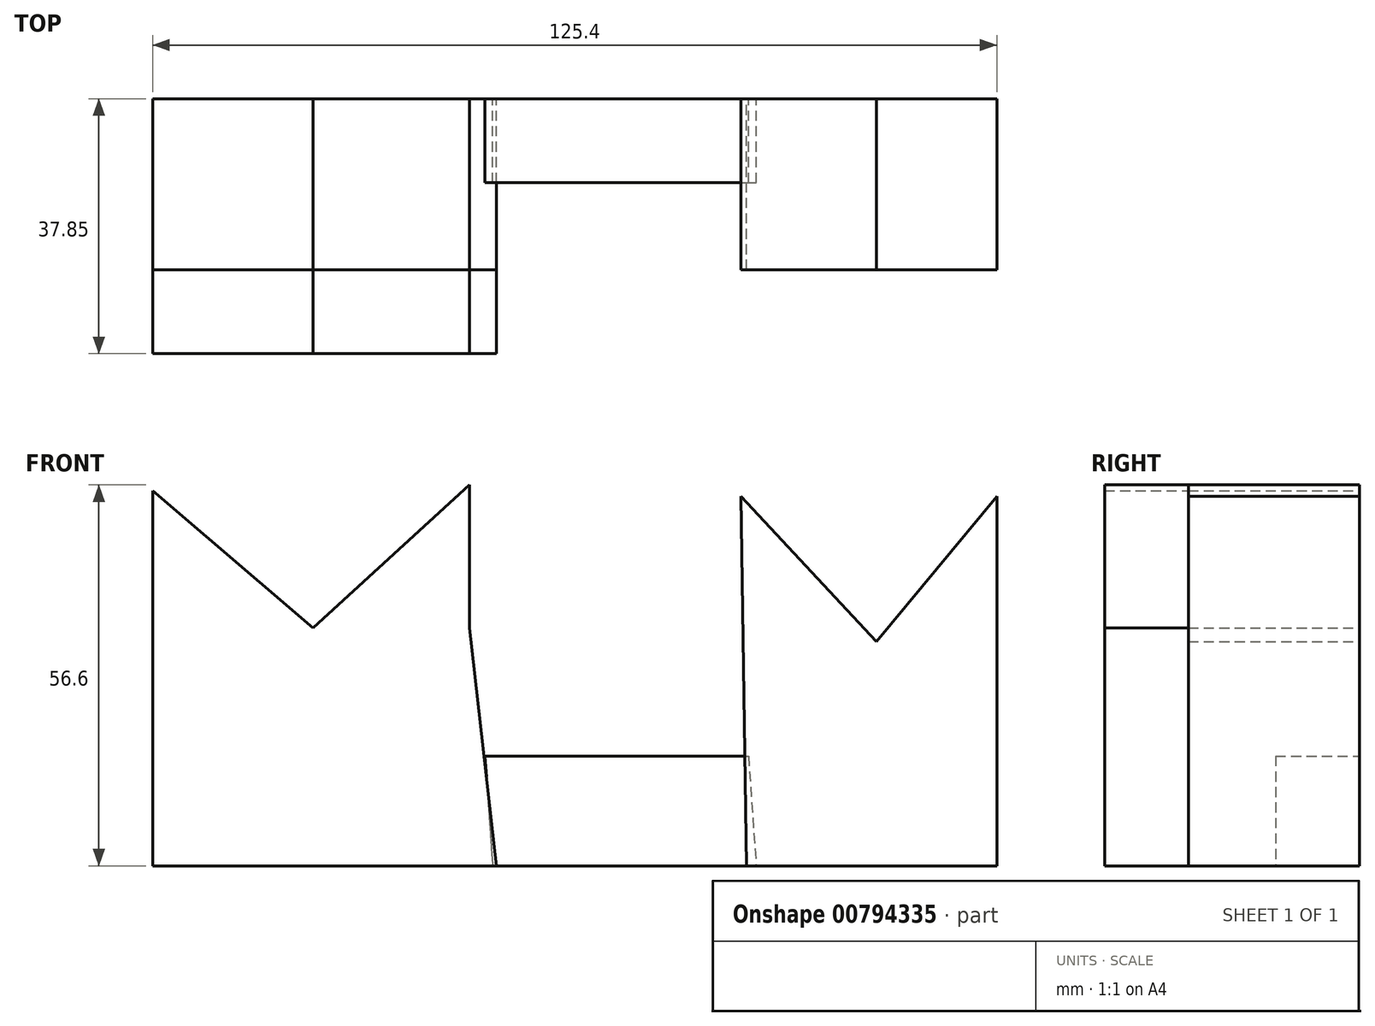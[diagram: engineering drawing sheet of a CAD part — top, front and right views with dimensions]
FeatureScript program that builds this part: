
annotation { "Feature Type Name" : "Feature", "Feature Type Description" : "" }
export const myFeature = defineFeature(function(context is Context, id is Id, definition is map)
    precondition{}
    {
        {
            var Q0;
            Q0=qCreatedBy(makeId("Front.planeOp"),FACE);
            var sketch = newSketch(context, id + "F0", { "sketchPlane" : qUnion([Q0])});
            skLineSegment(sketch, "E0", {"start": v(-26.24, 55.75) * mm, "end": v(-26.24, 0) * mm});
            skLineSegment(sketch, "E1", {"start": v(-26.24, 0) * mm, "end": v(24.83, 0) * mm});
            skLineSegment(sketch, "E2", {"start": v(24.83, 0) * mm, "end": v(20.85, 35.32) * mm});
            skLineSegment(sketch, "E3", {"start": v(20.85, 35.32) * mm, "end": v(20.85, 56.6) * mm});
            skLineSegment(sketch, "E4", {"start": v(-26.24, 55.75) * mm, "end": v(-2.41, 35.32) * mm});
            skLineSegment(sketch, "E5", {"start": v(20.85, 56.6) * mm, "end": v(-2.41, 35.32) * mm});
            skSolve(sketch);
        }
        {
            var Q0;
            Q0=makeQuery(id+"F0.imprint","IMPRINT",FACE,{"disambiguationData":[TD([[makeQuery(id+"F0.imprint","IMPRINT",EDGE,{"derivedFrom":sQuery(id+"F0.wireOp",EDGE,"E0")}),1.0]])]});
            var sketch = newSketch(context, id + "F1", { "sketchPlane" : qUnion([Q0])});
            skLineSegment(sketch, "E6", {"start": v(23.7, 17.73) * mm, "end": v(61.14, 17.73) * mm});
            skLineSegment(sketch, "E7", {"start": v(24.83, 0) * mm, "end": v(62, 0) * mm});
            skLineSegment(sketch, "E8", {"start": v(62, 0) * mm, "end": v(61.14, 54.9) * mm});
            skLineSegment(sketch, "E9", {"start": v(61.14, 54.9) * mm, "end": v(81.29, 33.34) * mm});
            skLineSegment(sketch, "E10", {"start": v(81.29, 33.34) * mm, "end": v(99.16, 54.9) * mm});
            skLineSegment(sketch, "E11", {"start": v(99.16, 54.9) * mm, "end": v(99.16, 0) * mm});
            skLineSegment(sketch, "E12", {"start": v(62, 0) * mm, "end": v(99.16, 0) * mm});
            skLineSegment(sketch, "E13", {"start": v(23.7, 17.73) * mm, "end": v(24.83, 0) * mm});
            skSolve(sketch);
        }
        {
            var Q0;
            Q0 = qSketchRegion(id + "F1", true);
            var Q1;
            Q1=makeQuery(id+"F0.imprint","IMPRINT",FACE,{"disambiguationData":[TD([[makeQuery(id+"F0.imprint","IMPRINT",EDGE,{"derivedFrom":sQuery(id+"F0.wireOp",EDGE,"E0")}),1.0]])]});
            extrude(context, id + "F2", {"entities" : qUnion([Q0, Q1]), "depth" : 25.4 * mm, "offsetDistance" : 25.4 * mm});
        }
        {
            var Q0;
            Q0=qCreatedBy(makeId("Front.planeOp"),FACE);
            var sketch = newSketch(context, id + "F3", { "sketchPlane" : qUnion([Q0])});
            skLineSegment(sketch, "E14", {"start": v(24.26, 0) * mm, "end": v(63.41, 0) * mm});
            skLineSegment(sketch, "E15", {"start": v(23.12, 16.31) * mm, "end": v(62.28, 16.31) * mm});
            skLineSegment(sketch, "E16", {"start": v(23.12, 16.31) * mm, "end": v(24.26, 0) * mm});
            skLineSegment(sketch, "E17", {"start": v(62.28, 16.31) * mm, "end": v(63.41, 0) * mm});
            skSolve(sketch);
        }
        {
            var Q0;
            Q0 = qSketchRegion(id + "F3", true);
            var Q1;
            Q1=makeQuery(id+"F2.opExtrude","CAP_FACE",FACE,{"disambiguationData":[OSD([sQuery(id+"F0.wireOp",EDGE,"E0"),sQuery(id+"F0.wireOp",EDGE,"E1"),sQuery(id+"F0.wireOp",EDGE,"E2"),sQuery(id+"F0.wireOp",EDGE,"E3"),sQuery(id+"F0.wireOp",EDGE,"E4"),sQuery(id+"F0.wireOp",EDGE,"E5")])],"isStart":false});
            extrude(context, id + "F4", {"entities" : qUnion([Q0, Q1]), "depth" : 12.45 * mm, "offsetDistance" : 25.4 * mm});
        }
    });
